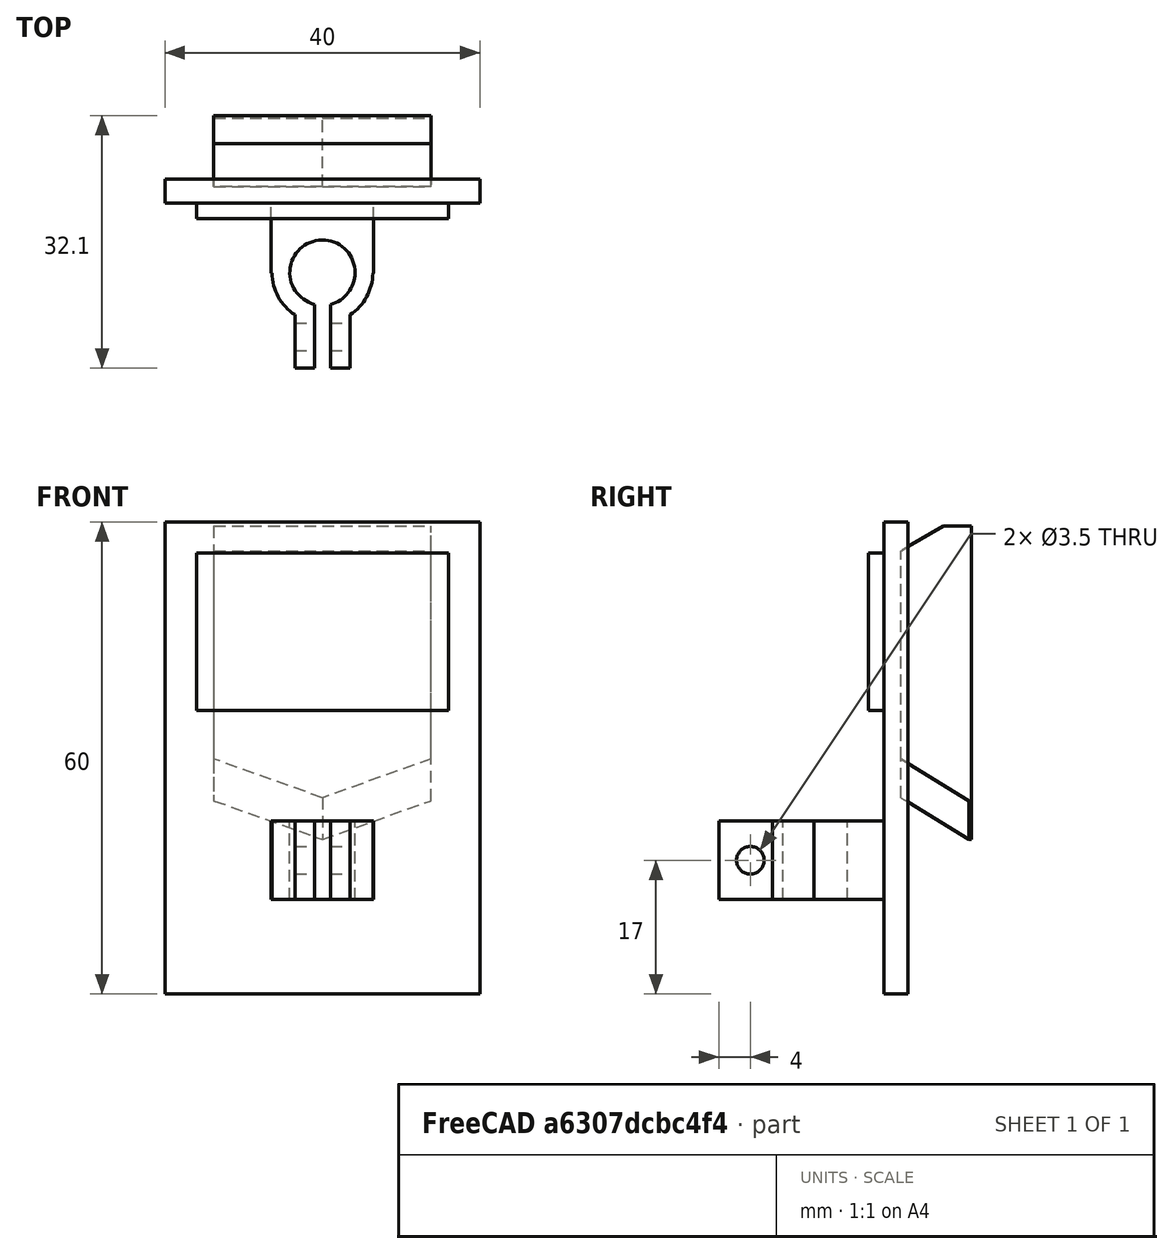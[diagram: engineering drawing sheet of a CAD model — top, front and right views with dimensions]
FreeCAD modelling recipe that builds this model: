
FCSTD DOCUMENT  (FreeCAD 0.18.4R)
Label: quicktool-comparator-mount
License: All rights reserved
LicenseURL: http://en.wikipedia.org/wiki/All_rights_reserved
objects: Part::Cut×7, Part::Box×6, Part::Cylinder×4, Part::Feature×1
note: 18 computed .brp shape members not serialized (recipe doc carries the construction recipe); baked Part::Feature solids carry a one-line shape summary decoded from their .brp

FEATURE [Part::Box] Box  label="Cube"
  AttacherType = Attacher::AttachEngine3D
  Height = 60
  Length = 40
  Placement = pos=(5,0,0) rot=(0,0,1;0rad)
  Width = 3
FEATURE [Part::Box] Box001  label="Cube001"
  AttacherType = Attacher::AttachEngine3D
  Height = 10
  Length = 13
  Placement = pos=(18.5,-19,0) rot=(0,0,1;0rad)
  Width = 21
FEATURE [Part::Cylinder] Cylinder
  Angle = 360
  AttacherType = Attacher::AttachEngine3D
  Height = 22
  Placement = pos=(25,-6.85,-3) rot=(0,0,1;0rad)
  Radius = 4.15
FEATURE [Part::Cylinder] Cylinder001
  Angle = 360
  AttacherType = Attacher::AttachEngine3D
  Height = 18
  Placement = pos=(16,-15,5) rot=(0,1,0;1.5708rad)
  Radius = 1.75
FEATURE [Part::Cylinder] Cylinder002
  Angle = 90
  AttacherType = Attacher::AttachEngine3D
  Height = 22
  Placement = pos=(25,-6.85,-3) rot=(0,0,1;4.71239rad)
  Radius = 6.4
FEATURE [Part::Box] Box002  label="Cube002"
  AttacherType = Attacher::AttachEngine3D
  Height = 22
  Length = 2
  Placement = pos=(24,-21,-3) rot=(0,0,1;0rad)
  Width = 11
FEATURE [Part::Cut] Cut
  Base = -> Box001
  Tool = -> Cylinder
FEATURE [Part::Cut] Cut001
  Base = -> Cut
  Tool = -> Cylinder001
FEATURE [Part::Cut] Cut002
  Base = -> Cut001
  Tool = -> Box002
FEATURE [Part::Box] Box003  label="Cube003"
  AttacherType = Attacher::AttachEngine3D
  Height = 22
  Length = 10
  Placement = pos=(28.5,-19,-3) rot=(0,0,1;0rad)
  Width = 12.1
FEATURE [Part::Box] Box004  label="Cube004"
  AttacherType = Attacher::AttachEngine3D
  Height = 22
  Length = 10
  Placement = pos=(11.5,-19,-3) rot=(0,0,1;0rad)
  Width = 12.1
FEATURE [Part::Cylinder] Cylinder003
  Angle = 90
  AttacherType = Attacher::AttachEngine3D
  Height = 22
  Placement = pos=(25,-6.85,-3) rot=(0,0,-1;3.14159rad)
  Radius = 6.4
FEATURE [Part::Cut] Cut003
  Base = -> Box003
  Tool = -> Cylinder002
FEATURE [Part::Cut] Cut004
  Base = -> Box004
  Tool = -> Cylinder003
FEATURE [Part::Cut] Cut005
  Base = -> Cut002
  Tool = -> Cut003
FEATURE [Part::Cut] Cut006
  Base = -> Cut005
  Placement = pos=(0,-2,12) rot=(0,0,1;0rad)
  Tool = -> Cut004
FEATURE [Part::Feature] Part__Feature  label="Blank tool holder v1"
  Placement = pos=(147,-86,-112) rot=(1,0,0;1.5708rad)
  shape: bbox 27.6 x 9 x 39.8 mm, 10 faces (baked)
FEATURE [Part::Box] Box005  label="Cube005"
  AttacherType = Attacher::AttachEngine3D
  Height = 20
  Length = 32
  Placement = pos=(9,-2,36) rot=(0,0,1;0rad)
  Width = 2
